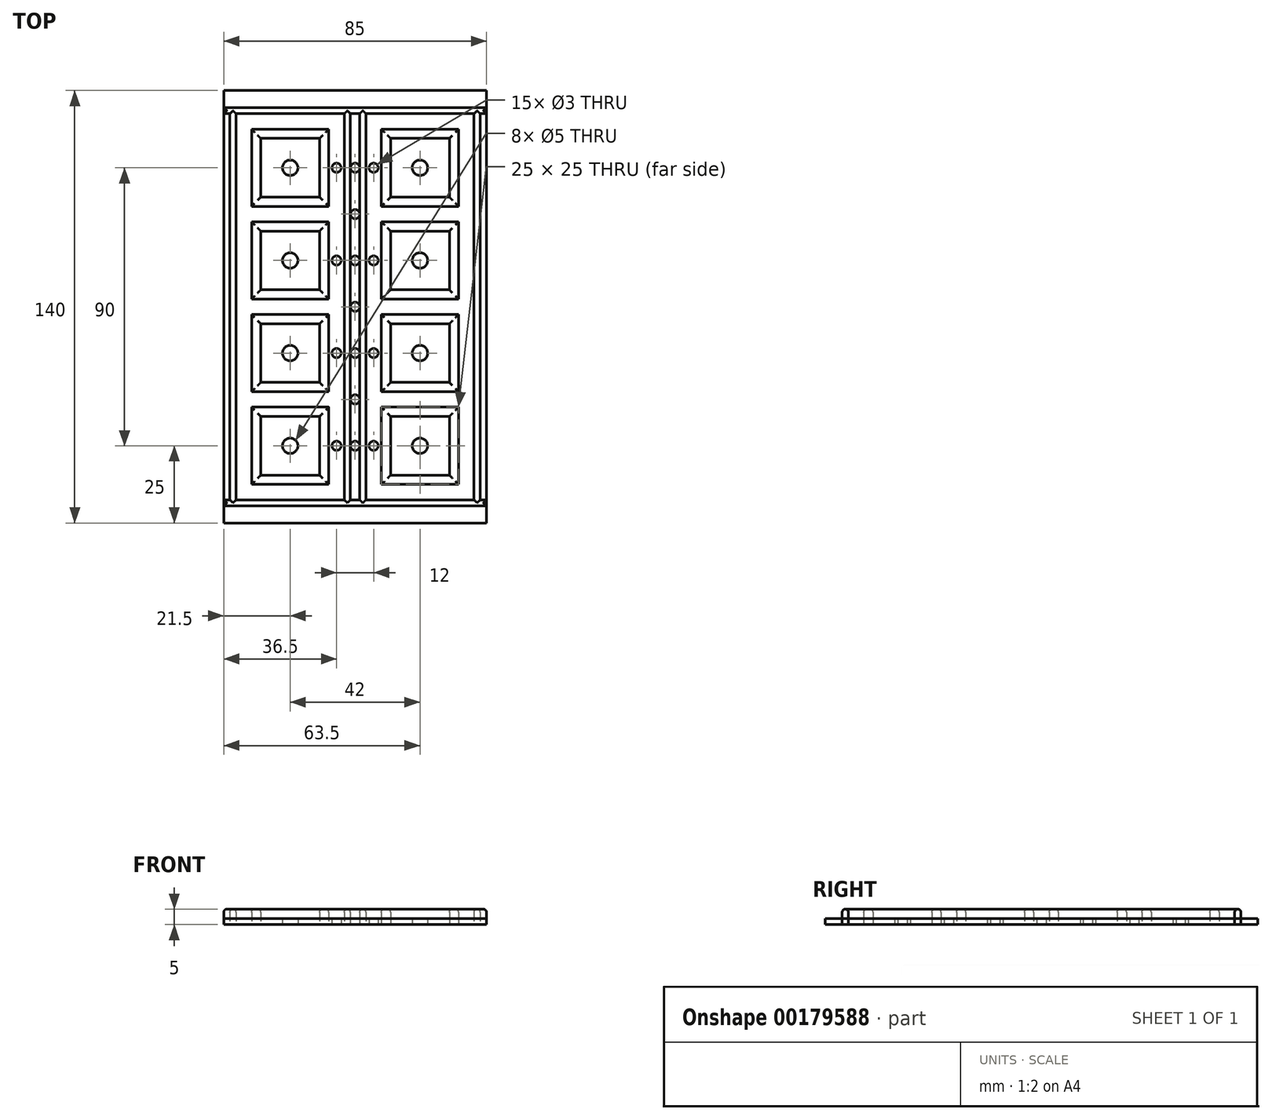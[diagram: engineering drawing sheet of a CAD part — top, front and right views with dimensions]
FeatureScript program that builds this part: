
annotation { "Feature Type Name" : "Feature", "Feature Type Description" : "" }
export const myFeature = defineFeature(function(context is Context, id is Id, definition is map)
    precondition{}
    {
        {
            var Q0;
            Q0=qCreatedBy(makeId("Top.planeOp"),FACE);
            var sketch = newSketch(context, id + "F0", { "sketchPlane" : qUnion([Q0])});
            skLineSegment(sketch, "E0.bottom", {"start": v(-42.5, -70) * mm, "end": v(42.5, -70) * mm});
            skLineSegment(sketch, "E0.top", {"start": v(-42.5, 70) * mm, "end": v(42.5, 70) * mm});
            skLineSegment(sketch, "E0.left", {"start": v(-42.5, -70) * mm, "end": v(-42.5, 70) * mm});
            skLineSegment(sketch, "E0.right", {"start": v(42.5, -70) * mm, "end": v(42.5, 70) * mm});
            skPoint(sketch, "E0.middle", {"position": v(0, 0) * mm});
            skLineSegment(sketch, "E1", {"start": v(0, -87.36) * mm, "end": v(0, 90.64) * mm, "construction": true});
            skPoint(sketch, "E1.startSnap0", {"position": v(0, 70) * mm});
            skLineSegment(sketch, "E2", {"start": v(0, 0) * mm, "end": v(42.5, 0) * mm, "construction": true});
            skLineSegment(sketch, "E3", {"start": v(38.5, 62.5) * mm, "end": v(38.5, -62.5) * mm});
            skLineSegment(sketch, "E4.MirrorCS", {"start": v(-42.5, -62.5) * mm, "end": v(42.5, -62.5) * mm});
            skLineSegment(sketch, "E5.bottom", {"start": v(8.5, 57.5) * mm, "end": v(33.5, 57.5) * mm});
            skLineSegment(sketch, "E5.top", {"start": v(8.5, 32.5) * mm, "end": v(33.5, 32.5) * mm});
            skLineSegment(sketch, "E5.left", {"start": v(8.5, 57.5) * mm, "end": v(8.5, 32.5) * mm});
            skLineSegment(sketch, "E5.right", {"start": v(33.5, 57.5) * mm, "end": v(33.5, 32.5) * mm});
            skLineSegment(sketch, "E6.bottom", {"start": v(8.5, 27.5) * mm, "end": v(33.5, 27.5) * mm});
            skLineSegment(sketch, "E6.top", {"start": v(8.5, 2.5) * mm, "end": v(33.5, 2.5) * mm});
            skLineSegment(sketch, "E6.left", {"start": v(8.5, 27.5) * mm, "end": v(8.5, 2.5) * mm});
            skLineSegment(sketch, "E6.right", {"start": v(33.5, 27.5) * mm, "end": v(33.5, 2.5) * mm});
            skLineSegment(sketch, "E7.0", {"start": v(11.5, 24.5) * mm, "end": v(30.5, 24.5) * mm});
            skLineSegment(sketch, "E7.1", {"start": v(11.5, 24.5) * mm, "end": v(11.5, 5.5) * mm});
            skLineSegment(sketch, "E7.2", {"start": v(11.5, 5.5) * mm, "end": v(30.5, 5.5) * mm});
            skLineSegment(sketch, "E7.3", {"start": v(30.5, 24.5) * mm, "end": v(30.5, 5.5) * mm});
            skLineSegment(sketch, "E8.0", {"start": v(11.5, 54.5) * mm, "end": v(30.5, 54.5) * mm});
            skLineSegment(sketch, "E8.1", {"start": v(11.5, 54.5) * mm, "end": v(11.5, 35.5) * mm});
            skLineSegment(sketch, "E8.2", {"start": v(11.5, 35.5) * mm, "end": v(30.5, 35.5) * mm});
            skLineSegment(sketch, "E8.3", {"start": v(30.5, 54.5) * mm, "end": v(30.5, 35.5) * mm});
            skLineSegment(sketch, "E9.0", {"start": v(-42.5, 62.5) * mm, "end": v(42.5, 62.5) * mm});
            skLineSegment(sketch, "E10", {"start": v(3.5, 62.5) * mm, "end": v(3.5, -62.5) * mm});
            skLineSegment(sketch, "E11.0", {"start": v(1.5, -62.5) * mm, "end": v(1.5, 62.5) * mm});
            skLineSegment(sketch, "E12.0", {"start": v(-42.5, 64.5) * mm, "end": v(42.5, 64.5) * mm});
            skLineSegment(sketch, "E13.0", {"start": v(40.5, 62.5) * mm, "end": v(40.5, -62.5) * mm});
            skLineSegment(sketch, "E14.MirrorCS", {"start": v(11.5, -5.5) * mm, "end": v(30.5, -5.5) * mm});
            skLineSegment(sketch, "E15.MirrorCS", {"start": v(11.5, -35.5) * mm, "end": v(30.5, -35.5) * mm});
            skLineSegment(sketch, "E16.MirrorCS", {"start": v(11.5, -24.5) * mm, "end": v(11.5, -5.5) * mm});
            skLineSegment(sketch, "E17.MirrorCS", {"start": v(11.5, -54.5) * mm, "end": v(11.5, -35.5) * mm});
            skLineSegment(sketch, "E18.MirrorCS", {"start": v(11.5, -24.5) * mm, "end": v(30.5, -24.5) * mm});
            skLineSegment(sketch, "E19.MirrorCS", {"start": v(11.5, -54.5) * mm, "end": v(30.5, -54.5) * mm});
            skLineSegment(sketch, "E20.MirrorCS", {"start": v(30.5, -54.5) * mm, "end": v(30.5, -35.5) * mm});
            skLineSegment(sketch, "E21.MirrorCS", {"start": v(8.5, -27.5) * mm, "end": v(33.5, -27.5) * mm});
            skLineSegment(sketch, "E22.MirrorCS", {"start": v(33.5, -57.5) * mm, "end": v(33.5, -32.5) * mm});
            skLineSegment(sketch, "E23.MirrorCS", {"start": v(8.5, -57.5) * mm, "end": v(8.5, -32.5) * mm});
            skLineSegment(sketch, "E24.MirrorCS", {"start": v(8.5, -32.5) * mm, "end": v(33.5, -32.5) * mm});
            skLineSegment(sketch, "E25.MirrorCS", {"start": v(8.5, -57.5) * mm, "end": v(33.5, -57.5) * mm});
            skLineSegment(sketch, "E26.MirrorCS", {"start": v(33.5, -27.5) * mm, "end": v(33.5, -2.5) * mm});
            skLineSegment(sketch, "E27.MirrorCS", {"start": v(8.5, -27.5) * mm, "end": v(8.5, -2.5) * mm});
            skLineSegment(sketch, "E28.MirrorCS", {"start": v(30.5, -24.5) * mm, "end": v(30.5, -5.5) * mm});
            skLineSegment(sketch, "E29.MirrorCS", {"start": v(8.5, -2.5) * mm, "end": v(33.5, -2.5) * mm});
            skLineSegment(sketch, "E30.MirrorCS", {"start": v(-1.5, -62.5) * mm, "end": v(-1.5, 62.5) * mm});
            skLineSegment(sketch, "E31.MirrorCS", {"start": v(-3.5, 62.5) * mm, "end": v(-3.5, -62.5) * mm});
            skLineSegment(sketch, "E32.MirrorCS", {"start": v(-40.5, 62.5) * mm, "end": v(-40.5, -62.5) * mm});
            skLineSegment(sketch, "E33.MirrorCS", {"start": v(-38.5, 62.5) * mm, "end": v(-38.5, -62.5) * mm});
            skLineSegment(sketch, "E34.MirrorCS", {"start": v(-8.5, 57.5) * mm, "end": v(-8.5, 32.5) * mm});
            skLineSegment(sketch, "E35.MirrorCS", {"start": v(-30.5, 24.5) * mm, "end": v(-30.5, 5.5) * mm});
            skLineSegment(sketch, "E36.MirrorCS", {"start": v(-8.5, -27.5) * mm, "end": v(-8.5, -2.5) * mm});
            skLineSegment(sketch, "E37.MirrorCS", {"start": v(-11.5, -5.5) * mm, "end": v(-30.5, -5.5) * mm});
            skLineSegment(sketch, "E38.MirrorCS", {"start": v(-8.5, -57.5) * mm, "end": v(-8.5, -32.5) * mm});
            skLineSegment(sketch, "E39.MirrorCS", {"start": v(-11.5, 5.5) * mm, "end": v(-30.5, 5.5) * mm});
            skLineSegment(sketch, "E40.MirrorCS", {"start": v(-11.5, 35.5) * mm, "end": v(-30.5, 35.5) * mm});
            skLineSegment(sketch, "E41.MirrorCS", {"start": v(-30.5, -54.5) * mm, "end": v(-30.5, -35.5) * mm});
            skLineSegment(sketch, "E42.MirrorCS", {"start": v(-8.5, 27.5) * mm, "end": v(-8.5, 2.5) * mm});
            skLineSegment(sketch, "E43.MirrorCS", {"start": v(-33.5, -27.5) * mm, "end": v(-33.5, -2.5) * mm});
            skLineSegment(sketch, "E44.MirrorCS", {"start": v(-33.5, 27.5) * mm, "end": v(-33.5, 2.5) * mm});
            skLineSegment(sketch, "E45.MirrorCS", {"start": v(-11.5, -35.5) * mm, "end": v(-30.5, -35.5) * mm});
            skLineSegment(sketch, "E46.MirrorCS", {"start": v(-8.5, -27.5) * mm, "end": v(-33.5, -27.5) * mm});
            skLineSegment(sketch, "E47.MirrorCS", {"start": v(-8.5, 32.5) * mm, "end": v(-33.5, 32.5) * mm});
            skLineSegment(sketch, "E48.MirrorCS", {"start": v(-8.5, -57.5) * mm, "end": v(-33.5, -57.5) * mm});
            skLineSegment(sketch, "E49.MirrorCS", {"start": v(-11.5, 24.5) * mm, "end": v(-30.5, 24.5) * mm});
            skLineSegment(sketch, "E50.MirrorCS", {"start": v(-8.5, -2.5) * mm, "end": v(-33.5, -2.5) * mm});
            skLineSegment(sketch, "E51.MirrorCS", {"start": v(-11.5, -54.5) * mm, "end": v(-11.5, -35.5) * mm});
            skLineSegment(sketch, "E52.MirrorCS", {"start": v(-11.5, -54.5) * mm, "end": v(-30.5, -54.5) * mm});
            skLineSegment(sketch, "E53.MirrorCS", {"start": v(-11.5, -24.5) * mm, "end": v(-30.5, -24.5) * mm});
            skLineSegment(sketch, "E54.MirrorCS", {"start": v(-11.5, 24.5) * mm, "end": v(-11.5, 5.5) * mm});
            skLineSegment(sketch, "E55.MirrorCS", {"start": v(-8.5, 2.5) * mm, "end": v(-33.5, 2.5) * mm});
            skLineSegment(sketch, "E56.MirrorCS", {"start": v(-8.5, 57.5) * mm, "end": v(-33.5, 57.5) * mm});
            skLineSegment(sketch, "E57.MirrorCS", {"start": v(-33.5, -57.5) * mm, "end": v(-33.5, -32.5) * mm});
            skLineSegment(sketch, "E58.MirrorCS", {"start": v(-11.5, -24.5) * mm, "end": v(-11.5, -5.5) * mm});
            skLineSegment(sketch, "E59.MirrorCS", {"start": v(-33.5, 57.5) * mm, "end": v(-33.5, 32.5) * mm});
            skLineSegment(sketch, "E60.MirrorCS", {"start": v(-11.5, 54.5) * mm, "end": v(-11.5, 35.5) * mm});
            skLineSegment(sketch, "E61.MirrorCS", {"start": v(-30.5, -24.5) * mm, "end": v(-30.5, -5.5) * mm});
            skLineSegment(sketch, "E62.MirrorCS", {"start": v(-8.5, -32.5) * mm, "end": v(-33.5, -32.5) * mm});
            skLineSegment(sketch, "E63.MirrorCS", {"start": v(-11.5, 54.5) * mm, "end": v(-30.5, 54.5) * mm});
            skLineSegment(sketch, "E64.MirrorCS", {"start": v(-30.5, 54.5) * mm, "end": v(-30.5, 35.5) * mm});
            skLineSegment(sketch, "E65.MirrorCS", {"start": v(-8.5, 27.5) * mm, "end": v(-33.5, 27.5) * mm});
            skLineSegment(sketch, "E66.0", {"start": v(-42.5, -64.5) * mm, "end": v(42.5, -64.5) * mm});
            skCircle(sketch, "E67", {"center": v(21, 45) * mm, "radius": 2.5 * mm});
            skLineSegment(sketch, "E68", {"start": v(11.5, 54.5) * mm, "end": v(30.5, 35.5) * mm, "construction": true});
            skLineSegment(sketch, "E69", {"start": v(30.5, 54.5) * mm, "end": v(11.5, 35.5) * mm, "construction": true});
            skLineSegment(sketch, "E70.0.1.0", {"start": v(11.5, 24.5) * mm, "end": v(30.5, 5.5) * mm, "construction": true});
            skCircle(sketch, "E70.0.1.1", {"center": v(21, 15) * mm, "radius": 2.5 * mm});
            skLineSegment(sketch, "E70.0.1.2", {"start": v(30.5, 24.5) * mm, "end": v(11.5, 5.5) * mm, "construction": true});
            skLineSegment(sketch, "E70.0.2.0", {"start": v(11.5, -5.5) * mm, "end": v(30.5, -24.5) * mm, "construction": true});
            skCircle(sketch, "E70.0.2.1", {"center": v(21, -15) * mm, "radius": 2.5 * mm});
            skLineSegment(sketch, "E70.0.2.2", {"start": v(30.5, -5.5) * mm, "end": v(11.5, -24.5) * mm, "construction": true});
            skLineSegment(sketch, "E70.0.3.0", {"start": v(11.5, -35.5) * mm, "end": v(30.5, -54.5) * mm, "construction": true});
            skCircle(sketch, "E70.0.3.1", {"center": v(21, -45) * mm, "radius": 2.5 * mm});
            skLineSegment(sketch, "E70.0.3.2", {"start": v(30.5, -35.5) * mm, "end": v(11.5, -54.5) * mm, "construction": true});
            skLineSegment(sketch, "E70.1.0.0", {"start": v(-30.5, 54.5) * mm, "end": v(-11.5, 35.5) * mm, "construction": true});
            skCircle(sketch, "E70.1.0.1", {"center": v(-21, 45) * mm, "radius": 2.5 * mm});
            skLineSegment(sketch, "E70.1.0.2", {"start": v(-11.5, 54.5) * mm, "end": v(-30.5, 35.5) * mm, "construction": true});
            skLineSegment(sketch, "E70.1.1.0", {"start": v(-30.5, 24.5) * mm, "end": v(-11.5, 5.5) * mm, "construction": true});
            skCircle(sketch, "E70.1.1.1", {"center": v(-21, 15) * mm, "radius": 2.5 * mm});
            skLineSegment(sketch, "E70.1.1.2", {"start": v(-11.5, 24.5) * mm, "end": v(-30.5, 5.5) * mm, "construction": true});
            skLineSegment(sketch, "E70.1.2.0", {"start": v(-30.5, -5.5) * mm, "end": v(-11.5, -24.5) * mm, "construction": true});
            skCircle(sketch, "E70.1.2.1", {"center": v(-21, -15) * mm, "radius": 2.5 * mm});
            skLineSegment(sketch, "E70.1.2.2", {"start": v(-11.5, -5.5) * mm, "end": v(-30.5, -24.5) * mm, "construction": true});
            skLineSegment(sketch, "E70.1.3.0", {"start": v(-30.5, -35.5) * mm, "end": v(-11.5, -54.5) * mm, "construction": true});
            skCircle(sketch, "E70.1.3.1", {"center": v(-21, -45) * mm, "radius": 2.5 * mm});
            skLineSegment(sketch, "E70.1.3.2", {"start": v(-11.5, -35.5) * mm, "end": v(-30.5, -54.5) * mm, "construction": true});
            skLineSegment(sketch, "E70.direction1", {"start": v(11.5, 35.5) * mm, "end": v(-30.5, 35.5) * mm, "construction": true});
            skLineSegment(sketch, "E70.direction2", {"start": v(11.5, 35.5) * mm, "end": v(11.5, 5.5) * mm, "construction": true});
            skCircle(sketch, "E71", {"center": v(0, 0) * mm, "radius": 1.5 * mm});
            skCircle(sketch, "E72.0.1.0", {"center": v(0, 15) * mm, "radius": 1.5 * mm});
            skCircle(sketch, "E72.0.2.0", {"center": v(0, 30) * mm, "radius": 1.5 * mm});
            skCircle(sketch, "E72.0.3.0", {"center": v(0, 45) * mm, "radius": 1.5 * mm});
            skLineSegment(sketch, "E72.0.3.1", {"start": v(3.5, 62.5) * mm, "end": v(3.5, -17.5) * mm});
            skLineSegment(sketch, "E72.direction1", {"start": v(0, 0) * mm, "end": v(56.6, 0) * mm, "construction": true});
            skLineSegment(sketch, "E72.direction2", {"start": v(0, 0) * mm, "end": v(0, 15) * mm, "construction": true});
            skCircle(sketch, "E73.0.1.0", {"center": v(0, -15) * mm, "radius": 1.5 * mm});
            skCircle(sketch, "E73.0.2.0", {"center": v(0, -30) * mm, "radius": 1.5 * mm});
            skCircle(sketch, "E73.0.3.0", {"center": v(0, -45) * mm, "radius": 1.5 * mm});
            skLineSegment(sketch, "E73.direction1", {"start": v(0, 0) * mm, "end": v(25, 0) * mm, "construction": true});
            skLineSegment(sketch, "E73.direction2", {"start": v(0, 0) * mm, "end": v(0, -15) * mm, "construction": true});
            skCircle(sketch, "E74.1.0.0", {"center": v(-6, -45) * mm, "radius": 1.5 * mm});
            skCircle(sketch, "E74.1.0.1", {"center": v(-6, -15) * mm, "radius": 1.5 * mm});
            skCircle(sketch, "E74.1.0.2", {"center": v(-6, 15) * mm, "radius": 1.5 * mm});
            skCircle(sketch, "E74.1.0.3", {"center": v(-6, 45) * mm, "radius": 1.5 * mm});
            skLineSegment(sketch, "E74.direction1", {"start": v(0, -45) * mm, "end": v(-6, -45) * mm, "construction": true});
            skPoint(sketch, "E75.orphan", {"position": v(3.5, 107.5) * mm});
            skCircle(sketch, "E76.1.0.0", {"center": v(6, -45) * mm, "radius": 1.5 * mm});
            skCircle(sketch, "E76.1.0.1", {"center": v(6, -15) * mm, "radius": 1.5 * mm});
            skCircle(sketch, "E76.1.0.2", {"center": v(6, 15) * mm, "radius": 1.5 * mm});
            skCircle(sketch, "E76.1.0.3", {"center": v(6, 45) * mm, "radius": 1.5 * mm});
            skLineSegment(sketch, "E76.direction1", {"start": v(0, -45) * mm, "end": v(6, -45) * mm, "construction": true});
            skSolve(sketch);
        }
        {
            var Q0;
            {var subQ0=sQuery(id+"F0.wireOp",EDGE,"E32.MirrorCS");Q0=makeQuery(id+"F0.imprint","IMPRINT",FACE,{"disambiguationData":[TD([[makeQuery(id+"F0.imprint","IMPRINT",EDGE,{"derivedFrom":subQ0}),1.0]])]});}
            var Q1;
            Q1=makeQuery(id+"F0.imprint","IMPRINT",FACE,{"disambiguationData":[TD([[makeQuery(id+"F0.imprint","IMPRINT",EDGE,{"derivedFrom":sQuery(id+"F0.wireOp",EDGE,"E36.MirrorCS")}),1.0]])]});
            var Q2;
            Q2=makeQuery(id+"F0.imprint","IMPRINT",FACE,{"disambiguationData":[TD([[makeQuery(id+"F0.imprint","IMPRINT",EDGE,{"derivedFrom":sQuery(id+"F0.wireOp",EDGE,"E35.MirrorCS")}),-1.0]])]});
            var Q3;
            Q3=makeQuery(id+"F0.imprint","IMPRINT",FACE,{"disambiguationData":[TD([[makeQuery(id+"F0.imprint","IMPRINT",EDGE,{"derivedFrom":sQuery(id+"F0.wireOp",EDGE,"E6.bottom")}),-1.0]])]});
            var Q4;
            Q4=makeQuery(id+"F0.imprint","IMPRINT",FACE,{"disambiguationData":[TD([[makeQuery(id+"F0.imprint","IMPRINT",EDGE,{"derivedFrom":sQuery(id+"F0.wireOp",EDGE,"E14.MirrorCS")}),1.0]])]});
            var Q5;
            Q5=makeQuery(id+"F0.imprint","IMPRINT",FACE,{"disambiguationData":[TD([[makeQuery(id+"F0.imprint","IMPRINT",EDGE,{"derivedFrom":sQuery(id+"F0.wireOp",EDGE,"E15.MirrorCS")}),1.0]])]});
            var Q6;
            Q6=makeQuery(id+"F0.imprint","IMPRINT",FACE,{"disambiguationData":[TD([[makeQuery(id+"F0.imprint","IMPRINT",EDGE,{"derivedFrom":sQuery(id+"F0.wireOp",EDGE,"E38.MirrorCS")}),1.0]])]});
            var Q7;
            {var subQ0=sQuery(id+"F0.wireOp",EDGE,"E3");Q7=makeQuery(id+"F0.imprint","IMPRINT",FACE,{"disambiguationData":[TD([[makeQuery(id+"F0.imprint","IMPRINT",EDGE,{"derivedFrom":subQ0}),1.0]])]});}
            var Q8;
            {var subQ7=sQuery(id+"F0.wireOp",EDGE,"E66.0");Q8=makeQuery(id+"F0.imprint","IMPRINT",FACE,{"disambiguationData":[TD([[makeQuery(id+"F0.imprint","IMPRINT",EDGE,{"derivedFrom":subQ7}),1.0]])]});}
            var Q9;
            Q9=makeQuery(id+"F0.imprint","IMPRINT",FACE,{"disambiguationData":[TD([[makeQuery(id+"F0.imprint","IMPRINT",EDGE,{"derivedFrom":sQuery(id+"F0.wireOp",EDGE,"E5.bottom")}),-1.0]])]});
            var Q10;
            Q10=makeQuery(id+"F0.imprint","IMPRINT",FACE,{"disambiguationData":[TD([[makeQuery(id+"F0.imprint","IMPRINT",EDGE,{"derivedFrom":sQuery(id+"F0.wireOp",EDGE,"E34.MirrorCS")}),-1.0]])]});
            var Q11;
            {var subQ9=sQuery(id+"F0.wireOp",EDGE,"E12.0");Q11=makeQuery(id+"F0.imprint","IMPRINT",FACE,{"disambiguationData":[TD([[makeQuery(id+"F0.imprint","IMPRINT",EDGE,{"derivedFrom":subQ9}),-1.0]])]});}
            var Q12;
            {var subQ10=sQuery(id+"F0.wireOp",EDGE,"E10");Q12=makeQuery(id+"F0.imprint","IMPRINT",FACE,{"disambiguationData":[TD([[makeQuery(id+"F0.imprint","IMPRINT",EDGE,{"derivedFrom":subQ10}),-1.0]])]});}
            var Q13;
            {var subQ12=sQuery(id+"F0.wireOp",EDGE,"E31.MirrorCS");Q13=makeQuery(id+"F0.imprint","IMPRINT",FACE,{"disambiguationData":[TD([[makeQuery(id+"F0.imprint","IMPRINT",EDGE,{"derivedFrom":subQ12}),1.0]])]});}
            extrude(context, id + "F1", {"entities" : qUnion([Q0, Q1, Q2, Q3, Q4, Q5, Q6, Q7, Q8, Q9, Q10, Q11, Q12, Q13]), "depth" : 5 * mm});
        }
        {
            var Q0;
            Q0=makeQuery(id+"F1.opExtrude","CAP_FACE",FACE,{"disambiguationData":[OSD([sQuery(id+"F0.wireOp",EDGE,"E5.bottom"),sQuery(id+"F0.wireOp",EDGE,"E5.top"),sQuery(id+"F0.wireOp",EDGE,"E5.left"),sQuery(id+"F0.wireOp",EDGE,"E5.right"),sQuery(id+"F0.wireOp",EDGE,"E8.0"),sQuery(id+"F0.wireOp",EDGE,"E8.1"),sQuery(id+"F0.wireOp",EDGE,"E8.2"),sQuery(id+"F0.wireOp",EDGE,"E8.3")])],"isStart":false});
            var Q1;
            Q1=makeQuery(id+"F1.opExtrude","CAP_FACE",FACE,{"disambiguationData":[OSD([sQuery(id+"F0.wireOp",EDGE,"E6.bottom"),sQuery(id+"F0.wireOp",EDGE,"E6.top"),sQuery(id+"F0.wireOp",EDGE,"E6.left"),sQuery(id+"F0.wireOp",EDGE,"E6.right"),sQuery(id+"F0.wireOp",EDGE,"E7.0"),sQuery(id+"F0.wireOp",EDGE,"E7.1"),sQuery(id+"F0.wireOp",EDGE,"E7.2"),sQuery(id+"F0.wireOp",EDGE,"E7.3")])],"isStart":false});
            var Q2;
            Q2=makeQuery(id+"F1.opExtrude","CAP_FACE",FACE,{"disambiguationData":[OSD([sQuery(id+"F0.wireOp",EDGE,"E0.left"),sQuery(id+"F0.wireOp",EDGE,"E0.right"),sQuery(id+"F0.wireOp",EDGE,"E3"),sQuery(id+"F0.wireOp",EDGE,"E4.MirrorCS"),sQuery(id+"F0.wireOp",EDGE,"E9.0"),sQuery(id+"F0.wireOp",EDGE,"E10"),sQuery(id+"F0.wireOp",EDGE,"E11.0"),sQuery(id+"F0.wireOp",EDGE,"E12.0"),sQuery(id+"F0.wireOp",EDGE,"E13.0"),sQuery(id+"F0.wireOp",EDGE,"E30.MirrorCS"),sQuery(id+"F0.wireOp",EDGE,"E31.MirrorCS"),sQuery(id+"F0.wireOp",EDGE,"E32.MirrorCS"),sQuery(id+"F0.wireOp",EDGE,"E33.MirrorCS"),sQuery(id+"F0.wireOp",EDGE,"E66.0"),sQuery(id+"F0.wireOp",EDGE,"E72.0.3.1")])],"isStart":false});
            var Q3;
            Q3=makeQuery(id+"F1.opExtrude","CAP_FACE",FACE,{"disambiguationData":[OSD([sQuery(id+"F0.wireOp",EDGE,"E34.MirrorCS"),sQuery(id+"F0.wireOp",EDGE,"E40.MirrorCS"),sQuery(id+"F0.wireOp",EDGE,"E47.MirrorCS"),sQuery(id+"F0.wireOp",EDGE,"E56.MirrorCS"),sQuery(id+"F0.wireOp",EDGE,"E59.MirrorCS"),sQuery(id+"F0.wireOp",EDGE,"E60.MirrorCS"),sQuery(id+"F0.wireOp",EDGE,"E63.MirrorCS"),sQuery(id+"F0.wireOp",EDGE,"E64.MirrorCS")])],"isStart":false});
            var Q4;
            Q4=makeQuery(id+"F1.opExtrude","CAP_FACE",FACE,{"disambiguationData":[OSD([sQuery(id+"F0.wireOp",EDGE,"E35.MirrorCS"),sQuery(id+"F0.wireOp",EDGE,"E39.MirrorCS"),sQuery(id+"F0.wireOp",EDGE,"E42.MirrorCS"),sQuery(id+"F0.wireOp",EDGE,"E44.MirrorCS"),sQuery(id+"F0.wireOp",EDGE,"E49.MirrorCS"),sQuery(id+"F0.wireOp",EDGE,"E54.MirrorCS"),sQuery(id+"F0.wireOp",EDGE,"E55.MirrorCS"),sQuery(id+"F0.wireOp",EDGE,"E65.MirrorCS")])],"isStart":false});
            var Q5;
            Q5=makeQuery(id+"F1.opExtrude","CAP_FACE",FACE,{"disambiguationData":[OSD([sQuery(id+"F0.wireOp",EDGE,"E36.MirrorCS"),sQuery(id+"F0.wireOp",EDGE,"E37.MirrorCS"),sQuery(id+"F0.wireOp",EDGE,"E43.MirrorCS"),sQuery(id+"F0.wireOp",EDGE,"E46.MirrorCS"),sQuery(id+"F0.wireOp",EDGE,"E50.MirrorCS"),sQuery(id+"F0.wireOp",EDGE,"E53.MirrorCS"),sQuery(id+"F0.wireOp",EDGE,"E58.MirrorCS"),sQuery(id+"F0.wireOp",EDGE,"E61.MirrorCS")])],"isStart":false});
            var Q6;
            Q6=makeQuery(id+"F1.opExtrude","CAP_FACE",FACE,{"disambiguationData":[OSD([sQuery(id+"F0.wireOp",EDGE,"E14.MirrorCS"),sQuery(id+"F0.wireOp",EDGE,"E16.MirrorCS"),sQuery(id+"F0.wireOp",EDGE,"E18.MirrorCS"),sQuery(id+"F0.wireOp",EDGE,"E21.MirrorCS"),sQuery(id+"F0.wireOp",EDGE,"E26.MirrorCS"),sQuery(id+"F0.wireOp",EDGE,"E27.MirrorCS"),sQuery(id+"F0.wireOp",EDGE,"E28.MirrorCS"),sQuery(id+"F0.wireOp",EDGE,"E29.MirrorCS")])],"isStart":false});
            var Q7;
            Q7=makeQuery(id+"F1.opExtrude","CAP_FACE",FACE,{"disambiguationData":[OSD([sQuery(id+"F0.wireOp",EDGE,"E15.MirrorCS"),sQuery(id+"F0.wireOp",EDGE,"E17.MirrorCS"),sQuery(id+"F0.wireOp",EDGE,"E19.MirrorCS"),sQuery(id+"F0.wireOp",EDGE,"E20.MirrorCS"),sQuery(id+"F0.wireOp",EDGE,"E22.MirrorCS"),sQuery(id+"F0.wireOp",EDGE,"E23.MirrorCS"),sQuery(id+"F0.wireOp",EDGE,"E24.MirrorCS"),sQuery(id+"F0.wireOp",EDGE,"E25.MirrorCS")])],"isStart":false});
            var Q8;
            Q8=makeQuery(id+"F1.opExtrude","CAP_FACE",FACE,{"disambiguationData":[OSD([sQuery(id+"F0.wireOp",EDGE,"E38.MirrorCS"),sQuery(id+"F0.wireOp",EDGE,"E41.MirrorCS"),sQuery(id+"F0.wireOp",EDGE,"E45.MirrorCS"),sQuery(id+"F0.wireOp",EDGE,"E48.MirrorCS"),sQuery(id+"F0.wireOp",EDGE,"E51.MirrorCS"),sQuery(id+"F0.wireOp",EDGE,"E52.MirrorCS"),sQuery(id+"F0.wireOp",EDGE,"E57.MirrorCS"),sQuery(id+"F0.wireOp",EDGE,"E62.MirrorCS")])],"isStart":false});
            fillet(context, id + "F2", {"entities" : qUnion([Q0, Q1, Q2, Q3, Q4, Q5, Q6, Q7, Q8]), "radius" : 1 * mm, "tangentPropagation" : true, "allowEdgeOverflow" : false});
        }
        {
            var Q0;
            {var subQ0=sQuery(id+"F0.wireOp",EDGE,"E0.bottom");Q0=makeQuery(id+"F0.imprint","IMPRINT",FACE,{"disambiguationData":[TD([[makeQuery(id+"F0.imprint","IMPRINT",EDGE,{"derivedFrom":subQ0}),1.0]])]});}
            var Q1;
            {var subQ7=sQuery(id+"F0.wireOp",EDGE,"E66.0");Q1=makeQuery(id+"F0.imprint","IMPRINT",FACE,{"disambiguationData":[TD([[makeQuery(id+"F0.imprint","IMPRINT",EDGE,{"derivedFrom":subQ7}),1.0]])]});}
            var Q2;
            {var subQ0=sQuery(id+"F0.wireOp",EDGE,"E32.MirrorCS");Q2=makeQuery(id+"F0.imprint","IMPRINT",FACE,{"disambiguationData":[TD([[makeQuery(id+"F0.imprint","IMPRINT",EDGE,{"derivedFrom":subQ0}),1.0]])]});}
            var Q3;
            {var subQ5=sQuery(id+"F0.wireOp",EDGE,"E32.MirrorCS");Q3=makeQuery(id+"F0.imprint","IMPRINT",FACE,{"disambiguationData":[TD([[makeQuery(id+"F0.imprint","IMPRINT",EDGE,{"derivedFrom":subQ5}),-1.0]])]});}
            var Q4;
            {var subQ1=sQuery(id+"F0.wireOp",EDGE,"E31.MirrorCS");Q4=makeQuery(id+"F0.imprint","IMPRINT",FACE,{"disambiguationData":[TD([[makeQuery(id+"F0.imprint","IMPRINT",EDGE,{"derivedFrom":subQ1}),-1.0]])]});}
            var Q5;
            Q5=makeQuery(id+"F0.imprint","IMPRINT",FACE,{"disambiguationData":[TD([[makeQuery(id+"F0.imprint","IMPRINT",EDGE,{"derivedFrom":sQuery(id+"F0.wireOp",EDGE,"E38.MirrorCS")}),1.0]])]});
            var Q6;
            Q6=makeQuery(id+"F0.imprint","IMPRINT",FACE,{"disambiguationData":[TD([[makeQuery(id+"F0.imprint","IMPRINT",EDGE,{"derivedFrom":sQuery(id+"F0.wireOp",EDGE,"E41.MirrorCS")}),-1.0]])]});
            var Q7;
            {var subQ12=sQuery(id+"F0.wireOp",EDGE,"E31.MirrorCS");Q7=makeQuery(id+"F0.imprint","IMPRINT",FACE,{"disambiguationData":[TD([[makeQuery(id+"F0.imprint","IMPRINT",EDGE,{"derivedFrom":subQ12}),1.0]])]});}
            var Q8;
            {var subQ0=sQuery(id+"F0.wireOp",EDGE,"E11.0");var subQ1=sQuery(id+"F0.wireOp",EDGE,"E4.MirrorCS");var subQ2=makeQuery(id+"F0.imprint","INTERSECT",VERTEX,{"derivedFrom":[subQ1,subQ0]});Q8=makeQuery(id+"F0.imprint","IMPRINT",FACE,{"disambiguationData":[TD([[makeQuery(id+"F0.imprint","IMPRINT",EDGE,{"disambiguationData":[TD([[subQ2,1.0]])],"derivedFrom":subQ1}),1.0]])]});}
            var Q9;
            {var subQ0=sQuery(id+"F0.wireOp",EDGE,"E73.0.3.0");var subQ1=sQuery(id+"F0.wireOp",EDGE,"E11.0");var subQ2=makeQuery(id+"F0.imprint","INTERSECT",VERTEX,{"derivedFrom":[subQ1,subQ0]});Q9=makeQuery(id+"F0.imprint","IMPRINT",FACE,{"disambiguationData":[TD([[makeQuery(id+"F0.imprint","IMPRINT",EDGE,{"disambiguationData":[TD([[subQ2,-1.0]])],"derivedFrom":subQ1}),1.0]])]});}
            var Q10;
            {var subQ2=sQuery(id+"F0.wireOp",EDGE,"E3");Q10=makeQuery(id+"F0.imprint","IMPRINT",FACE,{"disambiguationData":[TD([[makeQuery(id+"F0.imprint","IMPRINT",EDGE,{"derivedFrom":subQ2}),-1.0]])]});}
            var Q11;
            Q11=makeQuery(id+"F0.imprint","IMPRINT",FACE,{"disambiguationData":[TD([[makeQuery(id+"F0.imprint","IMPRINT",EDGE,{"derivedFrom":sQuery(id+"F0.wireOp",EDGE,"E15.MirrorCS")}),-1.0]])]});
            var Q12;
            {var subQ10=sQuery(id+"F0.wireOp",EDGE,"E10");Q12=makeQuery(id+"F0.imprint","IMPRINT",FACE,{"disambiguationData":[TD([[makeQuery(id+"F0.imprint","IMPRINT",EDGE,{"derivedFrom":subQ10}),-1.0]])]});}
            var Q13;
            {var subQ0=sQuery(id+"F0.wireOp",EDGE,"E3");Q13=makeQuery(id+"F0.imprint","IMPRINT",FACE,{"disambiguationData":[TD([[makeQuery(id+"F0.imprint","IMPRINT",EDGE,{"derivedFrom":subQ0}),1.0]])]});}
            var Q14;
            {var subQ5=sQuery(id+"F0.wireOp",EDGE,"E13.0");Q14=makeQuery(id+"F0.imprint","IMPRINT",FACE,{"disambiguationData":[TD([[makeQuery(id+"F0.imprint","IMPRINT",EDGE,{"derivedFrom":subQ5}),1.0]])]});}
            var Q15;
            Q15=makeQuery(id+"F0.imprint","IMPRINT",FACE,{"disambiguationData":[TD([[makeQuery(id+"F0.imprint","IMPRINT",EDGE,{"derivedFrom":sQuery(id+"F0.wireOp",EDGE,"E36.MirrorCS")}),1.0]])]});
            var Q16;
            Q16=makeQuery(id+"F0.imprint","IMPRINT",FACE,{"disambiguationData":[TD([[makeQuery(id+"F0.imprint","IMPRINT",EDGE,{"derivedFrom":sQuery(id+"F0.wireOp",EDGE,"E37.MirrorCS")}),1.0]])]});
            var Q17;
            {var subQ0=sQuery(id+"F0.wireOp",EDGE,"E73.0.2.0");var subQ1=sQuery(id+"F0.wireOp",EDGE,"E11.0");var subQ2=makeQuery(id+"F0.imprint","INTERSECT",VERTEX,{"derivedFrom":[subQ1,subQ0]});Q17=makeQuery(id+"F0.imprint","IMPRINT",FACE,{"disambiguationData":[TD([[makeQuery(id+"F0.imprint","IMPRINT",EDGE,{"disambiguationData":[TD([[subQ2,-1.0]])],"derivedFrom":subQ1}),1.0]])]});}
            var Q18;
            {var subQ0=sQuery(id+"F0.wireOp",EDGE,"E73.0.1.0");var subQ1=sQuery(id+"F0.wireOp",EDGE,"E11.0");var subQ2=makeQuery(id+"F0.imprint","INTERSECT",VERTEX,{"derivedFrom":[subQ1,subQ0]});Q18=makeQuery(id+"F0.imprint","IMPRINT",FACE,{"disambiguationData":[TD([[makeQuery(id+"F0.imprint","IMPRINT",EDGE,{"disambiguationData":[TD([[subQ2,-1.0]])],"derivedFrom":subQ1}),1.0]])]});}
            var Q19;
            Q19=makeQuery(id+"F0.imprint","IMPRINT",FACE,{"disambiguationData":[TD([[makeQuery(id+"F0.imprint","IMPRINT",EDGE,{"derivedFrom":sQuery(id+"F0.wireOp",EDGE,"E14.MirrorCS")}),-1.0]])]});
            var Q20;
            Q20=makeQuery(id+"F0.imprint","IMPRINT",FACE,{"disambiguationData":[TD([[makeQuery(id+"F0.imprint","IMPRINT",EDGE,{"derivedFrom":sQuery(id+"F0.wireOp",EDGE,"E14.MirrorCS")}),1.0]])]});
            var Q21;
            Q21=makeQuery(id+"F0.imprint","IMPRINT",FACE,{"disambiguationData":[TD([[makeQuery(id+"F0.imprint","IMPRINT",EDGE,{"derivedFrom":sQuery(id+"F0.wireOp",EDGE,"E6.bottom")}),-1.0]])]});
            var Q22;
            Q22=makeQuery(id+"F0.imprint","IMPRINT",FACE,{"disambiguationData":[TD([[makeQuery(id+"F0.imprint","IMPRINT",EDGE,{"derivedFrom":sQuery(id+"F0.wireOp",EDGE,"E7.0")}),-1.0]])]});
            var Q23;
            {var subQ0=sQuery(id+"F0.wireOp",EDGE,"E71");var subQ1=sQuery(id+"F0.wireOp",EDGE,"E11.0");var subQ2=makeQuery(id+"F0.imprint","INTERSECT",VERTEX,{"derivedFrom":[subQ1,subQ0]});Q23=makeQuery(id+"F0.imprint","IMPRINT",FACE,{"disambiguationData":[TD([[makeQuery(id+"F0.imprint","IMPRINT",EDGE,{"disambiguationData":[TD([[subQ2,-1.0]])],"derivedFrom":subQ1}),1.0]])]});}
            var Q24;
            {var subQ0=sQuery(id+"F0.wireOp",EDGE,"E72.0.1.0");var subQ1=sQuery(id+"F0.wireOp",EDGE,"E11.0");var subQ2=makeQuery(id+"F0.imprint","INTERSECT",VERTEX,{"derivedFrom":[subQ1,subQ0]});Q24=makeQuery(id+"F0.imprint","IMPRINT",FACE,{"disambiguationData":[TD([[makeQuery(id+"F0.imprint","IMPRINT",EDGE,{"disambiguationData":[TD([[subQ2,-1.0]])],"derivedFrom":subQ1}),1.0]])]});}
            var Q25;
            Q25=makeQuery(id+"F0.imprint","IMPRINT",FACE,{"disambiguationData":[TD([[makeQuery(id+"F0.imprint","IMPRINT",EDGE,{"derivedFrom":sQuery(id+"F0.wireOp",EDGE,"E35.MirrorCS")}),1.0]])]});
            var Q26;
            Q26=makeQuery(id+"F0.imprint","IMPRINT",FACE,{"disambiguationData":[TD([[makeQuery(id+"F0.imprint","IMPRINT",EDGE,{"derivedFrom":sQuery(id+"F0.wireOp",EDGE,"E35.MirrorCS")}),-1.0]])]});
            var Q27;
            Q27=makeQuery(id+"F0.imprint","IMPRINT",FACE,{"disambiguationData":[TD([[makeQuery(id+"F0.imprint","IMPRINT",EDGE,{"derivedFrom":sQuery(id+"F0.wireOp",EDGE,"E34.MirrorCS")}),-1.0]])]});
            var Q28;
            Q28=makeQuery(id+"F0.imprint","IMPRINT",FACE,{"disambiguationData":[TD([[makeQuery(id+"F0.imprint","IMPRINT",EDGE,{"derivedFrom":sQuery(id+"F0.wireOp",EDGE,"E40.MirrorCS")}),-1.0]])]});
            var Q29;
            {var subQ0=sQuery(id+"F0.wireOp",EDGE,"E72.0.2.0");var subQ1=sQuery(id+"F0.wireOp",EDGE,"E11.0");var subQ2=makeQuery(id+"F0.imprint","INTERSECT",VERTEX,{"derivedFrom":[subQ1,subQ0]});Q29=makeQuery(id+"F0.imprint","IMPRINT",FACE,{"disambiguationData":[TD([[makeQuery(id+"F0.imprint","IMPRINT",EDGE,{"disambiguationData":[TD([[subQ2,-1.0]])],"derivedFrom":subQ1}),1.0]])]});}
            var Q30;
            Q30=makeQuery(id+"F0.imprint","IMPRINT",FACE,{"disambiguationData":[TD([[makeQuery(id+"F0.imprint","IMPRINT",EDGE,{"derivedFrom":sQuery(id+"F0.wireOp",EDGE,"E5.bottom")}),-1.0]])]});
            var Q31;
            Q31=makeQuery(id+"F0.imprint","IMPRINT",FACE,{"disambiguationData":[TD([[makeQuery(id+"F0.imprint","IMPRINT",EDGE,{"derivedFrom":sQuery(id+"F0.wireOp",EDGE,"E8.0")}),-1.0]])]});
            var Q32;
            {var subQ0=sQuery(id+"F0.wireOp",EDGE,"E11.0");var subQ1=sQuery(id+"F0.wireOp",EDGE,"E9.0");var subQ2=makeQuery(id+"F0.imprint","INTERSECT",VERTEX,{"derivedFrom":[subQ1,subQ0]});Q32=makeQuery(id+"F0.imprint","IMPRINT",FACE,{"disambiguationData":[TD([[makeQuery(id+"F0.imprint","IMPRINT",EDGE,{"disambiguationData":[TD([[subQ2,1.0]])],"derivedFrom":subQ1}),-1.0]])]});}
            var Q33;
            {var subQ9=sQuery(id+"F0.wireOp",EDGE,"E12.0");Q33=makeQuery(id+"F0.imprint","IMPRINT",FACE,{"disambiguationData":[TD([[makeQuery(id+"F0.imprint","IMPRINT",EDGE,{"derivedFrom":subQ9}),-1.0]])]});}
            var Q34;
            {var subQ0=sQuery(id+"F0.wireOp",EDGE,"E0.top");Q34=makeQuery(id+"F0.imprint","IMPRINT",FACE,{"disambiguationData":[TD([[makeQuery(id+"F0.imprint","IMPRINT",EDGE,{"derivedFrom":subQ0}),-1.0]])]});}
            extrude(context, id + "F3", {"entities" : qUnion([Q0, Q1, Q2, Q3, Q4, Q5, Q6, Q7, Q8, Q9, Q10, Q11, Q12, Q13, Q14, Q15, Q16, Q17, Q18, Q19, Q20, Q21, Q22, Q23, Q24, Q25, Q26, Q27, Q28, Q29, Q30, Q31, Q32, Q33, Q34]), "depth" : 2 * mm});
        }
    });
